# Revit family: AB-QM 4.0_TP_Novocon_CO6_Novocon Actuator_RFA_1
name_source: partatom
category: Pipe Accessories
units: mm (PartAtom-declared; Revit-internal decimal feet)

## family parameters
Always vertical = Yes
Cut with Voids When Loaded = No
Part Type = Normal
Round Connector Dimension = Use Diameter
Shared = No
Work Plane-Based = No

## types (2) — shared parameters
A = 20.00°
Description = PICV and Motorized 6-port Ball Valves
H1 = 50 mm  [stored 0.164042 ft]
IfcExportAs = IfcValveType
IfcExportType = Changeover6 and AB-QM set
LOD 200 = No
LOD 350 = Yes
Manufacturer = Danfoss

## per-type parameters (varying)
| type | AB-QM size | CO6 size | D | L1 | L2 | Tailpiece size |
| AB-QM 4.0_Novocon_CO6_DN15 | AB-QM 4.0_DN15LF-DN20HF_External_TP_NovoCon_RFA : AB-QM_DN15NF_External_TP_003Z8201 | ChangeOver6_DN15-DN20_Novocon Actuator_RFA : ChangeOver6_DN15_003Z3150 | 15 mm  [stored 0.0492126 ft] | 9 mm  [stored 0.0295276 ft] | 53 mm  [stored 0.173885 ft] | Tailpiece_DN15-20_RFA : Short Tailpiece_DN15_003Z0232 |
| AB-QM 4.0_Novocon_CO6_DN20 | AB-QM 4.0_DN15LF-DN20HF_External_TP_NovoCon_RFA : AB-QM_DN20NF_External_TP_003Z8203 | ChangeOver6_DN15-DN20_Novocon Actuator_RFA : ChangeOver6_DN20_003Z3151 | 20 mm  [stored 0.0656168 ft] | 12 mm  [stored 0.0393701 ft] | 60 mm  [stored 0.19685 ft] | Tailpiece_DN15-20_RFA : Short Tailpiece_DN20_003Z0233 |

note: column(s) folded — value = type name in every type: Model Type

note: [stored X ft] marks values corroborated as IEEE doubles in the binary element streams (Revit-internal decimal feet)

## geometry (parser evidence)
native form markers: Blend x8, Sweep x11
no freeform markers — native parametric forms only
